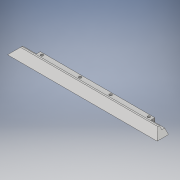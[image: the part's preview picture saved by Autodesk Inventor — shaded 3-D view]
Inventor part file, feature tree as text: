
AUTODESK INVENTOR PART (.ipt)
format: ipt  version: 2019 (Build 230136000, 136)  size: 139,776 bytes
history: native  units: mm
features: sketch x3, extrude x3, other x1, hole x1
ambient origin geometry x8: Origin, YZ Plane, XZ Plane, XY Plane, X Axis, Y Axis, Z Axis, Center Point
bodies: Body1 (feature_tree)
feature tree (8):
  other  "Bryła1"
  sketch  "Szkic1"
  extrude  "Wyciągnięcie proste1"  Depth=20.1mm
  extrude  "Wyciągnięcie proste2"  Depth=8.0mm
  hole  "Otwór1"  [1 undecoded]
  extrude  "Wyciągnięcie proste3"  Depth=5.2mm
  sketch  "Szkic3"
  sketch  "Szkic4"
note: 1 required parameter value undecoded (feature->parameter linkage not recoverable at this tier; creation-order binding heuristic only, values carry confidence <= 0.55)
